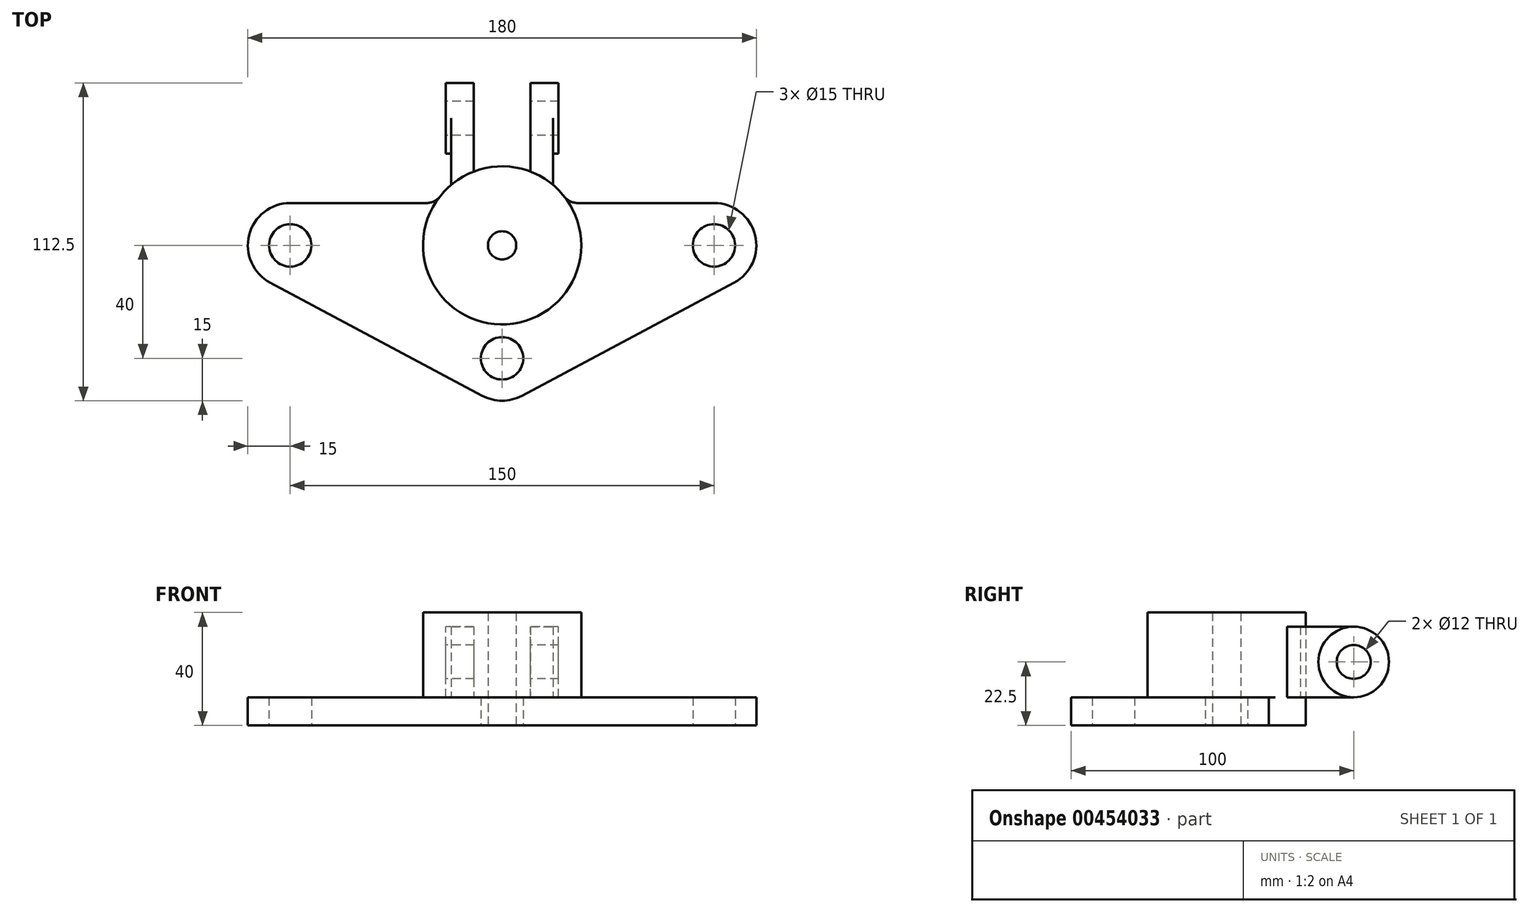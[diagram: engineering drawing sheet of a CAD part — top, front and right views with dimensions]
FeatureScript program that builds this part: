
annotation { "Feature Type Name" : "Feature", "Feature Type Description" : "" }
export const myFeature = defineFeature(function(context is Context, id is Id, definition is map)
    precondition{}
    {
        {
            var Q0;
            Q0=qCreatedBy(makeId("Top.planeOp"),FACE);
            var sketch = newSketch(context, id + "F0", { "sketchPlane" : qUnion([Q0])});
            skCircle(sketch, "E0", {"center": v(0, 0) * mm, "radius": 28 * mm});
            skArc(sketch, "E1", {"start": v(-7.06, -53.24) * mm, "mid": v(0, -55) * mm, "end": v(7.06, -53.24) * mm});
            skArc(sketch, "E2", {"start": v(82.06, -13.24) * mm, "mid": v(89.55, 3.64) * mm, "end": v(75, 15) * mm});
            skArc(sketch, "E3", {"start": v(-75, 15) * mm, "mid": v(-89.55, 3.64) * mm, "end": v(-82.06, -13.24) * mm});
            skLineSegment(sketch, "E4", {"start": v(-82.06, -13.24) * mm, "end": v(-7.06, -53.24) * mm});
            skLineSegment(sketch, "E5", {"start": v(7.06, -53.24) * mm, "end": v(82.06, -13.24) * mm});
            skLineSegment(sketch, "E6", {"start": v(75, 15) * mm, "end": v(26.74, 15) * mm});
            skLineSegment(sketch, "E7", {"start": v(-26.74, 15) * mm, "end": v(-75, 15) * mm});
            skCircle(sketch, "E8", {"center": v(0, 0) * mm, "radius": 5 * mm});
            skCircle(sketch, "E9", {"center": v(-75, 0) * mm, "radius": 7.5 * mm});
            skCircle(sketch, "E10", {"center": v(0, -40) * mm, "radius": 7.5 * mm});
            skCircle(sketch, "E11", {"center": v(75, 0) * mm, "radius": 7.5 * mm});
            skArc(sketch, "E12", {"start": v(22.02, 17.3) * mm, "mid": v(24.12, 15.6) * mm, "end": v(26.74, 15) * mm});
            skArc(sketch, "E13", {"start": v(-26.74, 15) * mm, "mid": v(-24.12, 15.6) * mm, "end": v(-22.02, 17.3) * mm});
            skSolve(sketch);
        }
        {
            var Q0;
            Q0=makeQuery(id+"F0.imprint","IMPRINT",FACE,{"disambiguationData":[TD([[makeQuery(id+"F0.imprint","IMPRINT",EDGE,{"derivedFrom":sQuery(id+"F0.wireOp",EDGE,"E1")}),1.0]])]});
            extrude(context, id + "F1", {"entities" : qUnion([Q0]), "depth" : 10 * mm});
        }
        {
            var Q0;
            Q0=makeQuery(id+"F0.imprint","IMPRINT",FACE,{"disambiguationData":[TD([[makeQuery(id+"F0.imprint","IMPRINT",EDGE,{"derivedFrom":sQuery(id+"F0.wireOp",EDGE,"E8")}),-1.0]])]});
            extrude(context, id + "F2", {"entities" : qUnion([Q0]), "operationType" : NewBodyOperationType.ADD, "depth" : 40 * mm});
        }
        {
            var Q0;
            Q0=qCreatedBy(makeId("Right.planeOp"),FACE);
            var sketch = newSketch(context, id + "F3", { "sketchPlane" : qUnion([Q0])});
            skLineSegment(sketch, "E14", {"start": v(45, 35) * mm, "end": v(15, 35) * mm});
            skLineSegment(sketch, "E15", {"start": v(15, 35) * mm, "end": v(15, 10) * mm});
            skLineSegment(sketch, "E16", {"start": v(15, 10) * mm, "end": v(45, 10) * mm});
            skArc(sketch, "E17", {"start": v(45, 10) * mm, "mid": v(57.5, 22.5) * mm, "end": v(45, 35) * mm});
            skCircle(sketch, "E18", {"center": v(45, 22.5) * mm, "radius": 6 * mm});
            skArc(sketch, "E19", {"start": v(45, 35) * mm, "mid": v(32.5, 22.5) * mm, "end": v(45, 10) * mm});
            skSolve(sketch);
        }
        {
            var Q0;
            Q0=makeQuery(id+"F3.imprint","IMPRINT",FACE,{"disambiguationData":[TD([[makeQuery(id+"F3.imprint","IMPRINT",EDGE,{"derivedFrom":sQuery(id+"F3.wireOp",EDGE,"E14")}),1.0]])]});
            var Q1;
            Q1=makeQuery(id+"F3.imprint","IMPRINT",FACE,{"disambiguationData":[TD([[makeQuery(id+"F3.imprint","IMPRINT",EDGE,{"derivedFrom":sQuery(id+"F3.wireOp",EDGE,"E17")}),1.0]])]});
            extrude(context, id + "F4", {"entities" : qUnion([Q0, Q1]), "operationType" : NewBodyOperationType.ADD, "endBound" : BoundingType.SYMMETRIC, "depth" : 36 * mm});
        }
        {
            var Q0;
            Q0=makeQuery(id+"F3.imprint","IMPRINT",FACE,{"disambiguationData":[TD([[makeQuery(id+"F3.imprint","IMPRINT",EDGE,{"derivedFrom":sQuery(id+"F3.wireOp",EDGE,"E17")}),1.0]])]});
            extrude(context, id + "F5", {"entities" : qUnion([Q0]), "operationType" : NewBodyOperationType.ADD, "endBound" : BoundingType.SYMMETRIC, "depth" : 40 * mm});
        }
        {
            var Q0;
            Q0=qCreatedBy(makeId("Top.planeOp"),FACE);
            var sketch = newSketch(context, id + "F6", { "sketchPlane" : qUnion([Q0])});
            skArc(sketch, "E20.0", {"start": v(10, 26.15) * mm, "mid": v(0, 28) * mm, "end": v(-10, 26.15) * mm});
            skLineSegment(sketch, "E21", {"start": v(-10, 26.15) * mm, "end": v(-10, 64.15) * mm});
            skLineSegment(sketch, "E22", {"start": v(-10, 64.15) * mm, "end": v(10, 64.15) * mm});
            skLineSegment(sketch, "E23", {"start": v(10, 64.15) * mm, "end": v(10, 26.15) * mm});
            skSolve(sketch);
        }
        {
            var Q0;
            Q0=makeQuery(id+"F6.imprint","IMPRINT",FACE,{"disambiguationData":[TD([[makeQuery(id+"F6.imprint","IMPRINT",EDGE,{"derivedFrom":sQuery(id+"F6.wireOp",EDGE,"E20.0")}),-1.0]])]});
            extrude(context, id + "F7", {"entities" : qUnion([Q0]), "operationType" : NewBodyOperationType.REMOVE, "endBound" : BoundingType.THROUGH_ALL, "depth" : 25 * mm});
        }
    });
